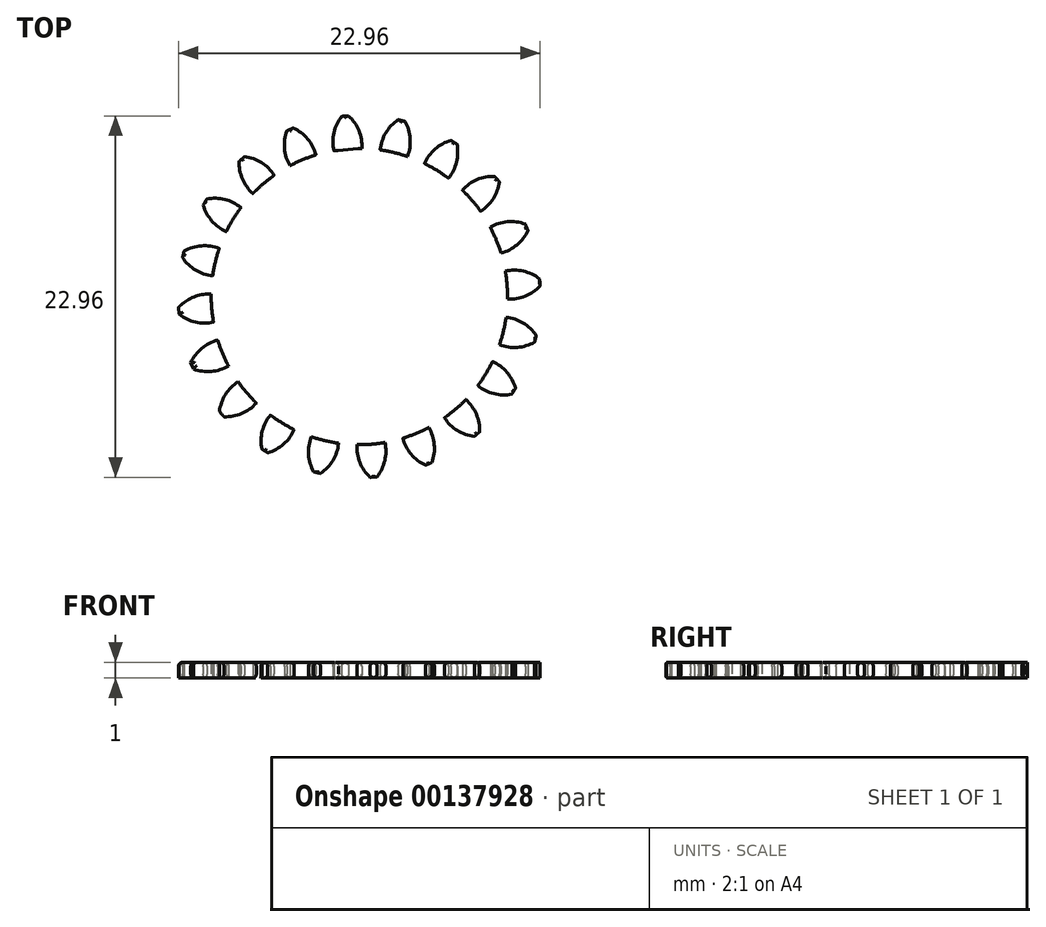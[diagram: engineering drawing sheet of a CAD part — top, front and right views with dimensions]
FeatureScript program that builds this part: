
annotation { "Feature Type Name" : "Feature", "Feature Type Description" : "" }
export const myFeature = defineFeature(function(context is Context, id is Id, definition is map)
    precondition{}
    {
        {
            assignVariable(context, id + "F0", {"name" : "GearDepth", "anyValue" : 1});
        }
        {
            assignVariable(context, id + "F1", {"name" : "TeethFillet", "anyValue" : getVariable(context, 'GearDepth') * .25});
        }
        {
            var Q0;
            Q0=qCreatedBy(makeId("Top.planeOp"),FACE);
            var sketch = newSketch(context, id + "F2", { "sketchPlane" : qUnion([Q0])});
            skCircle(sketch, "E0", {"center": v(0, 0) * mm, "radius": 9.4 * mm});
            skCircle(sketch, "E1", {"center": v(0, 0) * mm, "radius": 10.45 * mm, "construction": true});
            skCircle(sketch, "E2", {"center": v(0, 0) * mm, "radius": 11.5 * mm, "construction": true});
            skLineSegment(sketch, "E3", {"start": v(0, 0) * mm, "end": v(0, 17.6) * mm, "construction": true});
            skLineSegment(sketch, "E4", {"start": v(0, 0) * mm, "end": v(-1.42, 18) * mm, "construction": true});
            skLineSegment(sketch, "E5", {"start": v(0, 10.45) * mm, "end": v(-10.54, 10.45) * mm, "construction": true});
            skLineSegment(sketch, "E6", {"start": v(0, 10.45) * mm, "end": v(-10.3, 6.7) * mm, "construction": true});
            skCircle(sketch, "E7", {"center": v(0, 10.45) * mm, "radius": 2.61 * mm, "construction": true});
            skCircle(sketch, "E8", {"center": v(-2.46, 9.56) * mm, "radius": 2.61 * mm, "construction": true});
            skArc(sketch, "E9", {"start": v(-4.91, 10.45) * mm, "mid": v(-4.92, 10.42) * mm, "end": v(-4.94, 10.39) * mm});
            skArc(sketch, "E10.trimOffspring", {"start": v(0.15, 9.4) * mm, "mid": v(-0.03, 10.54) * mm, "end": v(-0.68, 11.48) * mm});
            skArc(sketch, "E11.MirrorCS", {"start": v(-1.62, 9.27) * mm, "mid": v(-1.62, 10.41) * mm, "end": v(-1.12, 11.45) * mm});
            skLineSegment(sketch, "E12", {"start": v(-1.12, 11.45) * mm, "end": v(-0.68, 11.48) * mm});
            skArc(sketch, "E13.1.0", {"start": v(-2.76, 9) * mm, "mid": v(-3.29, 10.01) * mm, "end": v(-4.2, 10.7) * mm});
            skLineSegment(sketch, "E13.1.1", {"start": v(-4.6, 10.54) * mm, "end": v(-4.2, 10.7) * mm});
            skArc(sketch, "E13.1.2", {"start": v(-4.4, 8.31) * mm, "mid": v(-4.76, 9.4) * mm, "end": v(-4.6, 10.54) * mm});
            skArc(sketch, "E13.2.0", {"start": v(-5.4, 7.7) * mm, "mid": v(-6.22, 8.5) * mm, "end": v(-7.3, 8.89) * mm});
            skLineSegment(sketch, "E13.2.1", {"start": v(-7.64, 8.6) * mm, "end": v(-7.3, 8.89) * mm});
            skArc(sketch, "E13.2.2", {"start": v(-6.76, 6.54) * mm, "mid": v(-7.43, 7.47) * mm, "end": v(-7.64, 8.6) * mm});
            skArc(sketch, "E13.3.0", {"start": v(-7.52, 5.65) * mm, "mid": v(-8.54, 6.17) * mm, "end": v(-9.69, 6.2) * mm});
            skLineSegment(sketch, "E13.3.1", {"start": v(-9.92, 5.82) * mm, "end": v(-9.69, 6.2) * mm});
            skArc(sketch, "E13.3.2", {"start": v(-8.45, 4.13) * mm, "mid": v(-9.37, 4.81) * mm, "end": v(-9.92, 5.82) * mm});
            skArc(sketch, "E13.4.0", {"start": v(-8.9, 3.05) * mm, "mid": v(-10.03, 3.23) * mm, "end": v(-11.13, 2.9) * mm});
            skLineSegment(sketch, "E13.4.1", {"start": v(-11.23, 2.47) * mm, "end": v(-11.13, 2.9) * mm});
            skArc(sketch, "E13.4.2", {"start": v(-9.32, 1.32) * mm, "mid": v(-10.4, 1.68) * mm, "end": v(-11.23, 2.47) * mm});
            skArc(sketch, "E13.5.0", {"start": v(-9.4, 0.15) * mm, "mid": v(-10.54, -0.03) * mm, "end": v(-11.48, -0.68) * mm});
            skLineSegment(sketch, "E13.5.1", {"start": v(-11.45, -1.12) * mm, "end": v(-11.48, -0.68) * mm});
            skArc(sketch, "E13.5.2", {"start": v(-9.27, -1.62) * mm, "mid": v(-10.41, -1.62) * mm, "end": v(-11.45, -1.12) * mm});
            skArc(sketch, "E13.6.0", {"start": v(-9, -2.76) * mm, "mid": v(-10.01, -3.29) * mm, "end": v(-10.7, -4.2) * mm});
            skLineSegment(sketch, "E13.6.1", {"start": v(-10.54, -4.6) * mm, "end": v(-10.7, -4.2) * mm});
            skArc(sketch, "E13.6.2", {"start": v(-8.31, -4.4) * mm, "mid": v(-9.4, -4.76) * mm, "end": v(-10.54, -4.6) * mm});
            skArc(sketch, "E13.7.0", {"start": v(-7.7, -5.4) * mm, "mid": v(-8.5, -6.22) * mm, "end": v(-8.89, -7.3) * mm});
            skLineSegment(sketch, "E13.7.1", {"start": v(-8.6, -7.64) * mm, "end": v(-8.89, -7.3) * mm});
            skArc(sketch, "E13.7.2", {"start": v(-6.54, -6.76) * mm, "mid": v(-7.47, -7.43) * mm, "end": v(-8.6, -7.64) * mm});
            skArc(sketch, "E13.8.0", {"start": v(-5.65, -7.52) * mm, "mid": v(-6.17, -8.54) * mm, "end": v(-6.2, -9.69) * mm});
            skLineSegment(sketch, "E13.8.1", {"start": v(-5.82, -9.92) * mm, "end": v(-6.2, -9.69) * mm});
            skArc(sketch, "E13.8.2", {"start": v(-4.13, -8.45) * mm, "mid": v(-4.81, -9.37) * mm, "end": v(-5.82, -9.92) * mm});
            skArc(sketch, "E13.9.0", {"start": v(-3.05, -8.9) * mm, "mid": v(-3.23, -10.03) * mm, "end": v(-2.9, -11.13) * mm});
            skLineSegment(sketch, "E13.9.1", {"start": v(-2.47, -11.23) * mm, "end": v(-2.9, -11.13) * mm});
            skArc(sketch, "E13.9.2", {"start": v(-1.32, -9.32) * mm, "mid": v(-1.68, -10.4) * mm, "end": v(-2.47, -11.23) * mm});
            skArc(sketch, "E13.10.0", {"start": v(-0.15, -9.4) * mm, "mid": v(0.03, -10.54) * mm, "end": v(0.68, -11.48) * mm});
            skLineSegment(sketch, "E13.10.1", {"start": v(1.12, -11.45) * mm, "end": v(0.68, -11.48) * mm});
            skArc(sketch, "E13.10.2", {"start": v(1.62, -9.27) * mm, "mid": v(1.62, -10.41) * mm, "end": v(1.12, -11.45) * mm});
            skArc(sketch, "E13.11.0", {"start": v(2.76, -9) * mm, "mid": v(3.29, -10.01) * mm, "end": v(4.2, -10.7) * mm});
            skLineSegment(sketch, "E13.11.1", {"start": v(4.6, -10.54) * mm, "end": v(4.2, -10.7) * mm});
            skArc(sketch, "E13.11.2", {"start": v(4.4, -8.31) * mm, "mid": v(4.76, -9.4) * mm, "end": v(4.6, -10.54) * mm});
            skArc(sketch, "E13.12.0", {"start": v(5.4, -7.7) * mm, "mid": v(6.22, -8.5) * mm, "end": v(7.3, -8.89) * mm});
            skLineSegment(sketch, "E13.12.1", {"start": v(7.64, -8.6) * mm, "end": v(7.3, -8.89) * mm});
            skArc(sketch, "E13.12.2", {"start": v(6.76, -6.54) * mm, "mid": v(7.43, -7.47) * mm, "end": v(7.64, -8.6) * mm});
            skArc(sketch, "E13.13.0", {"start": v(7.52, -5.65) * mm, "mid": v(8.54, -6.17) * mm, "end": v(9.69, -6.2) * mm});
            skLineSegment(sketch, "E13.13.1", {"start": v(9.92, -5.82) * mm, "end": v(9.69, -6.2) * mm});
            skArc(sketch, "E13.13.2", {"start": v(8.45, -4.13) * mm, "mid": v(9.37, -4.81) * mm, "end": v(9.92, -5.82) * mm});
            skArc(sketch, "E13.14.0", {"start": v(8.9, -3.05) * mm, "mid": v(10.03, -3.23) * mm, "end": v(11.13, -2.9) * mm});
            skLineSegment(sketch, "E13.14.1", {"start": v(11.23, -2.47) * mm, "end": v(11.13, -2.9) * mm});
            skArc(sketch, "E13.14.2", {"start": v(9.32, -1.32) * mm, "mid": v(10.4, -1.68) * mm, "end": v(11.23, -2.47) * mm});
            skArc(sketch, "E13.15.0", {"start": v(9.4, -0.15) * mm, "mid": v(10.54, 0.03) * mm, "end": v(11.48, 0.68) * mm});
            skLineSegment(sketch, "E13.15.1", {"start": v(11.45, 1.12) * mm, "end": v(11.48, 0.68) * mm});
            skArc(sketch, "E13.15.2", {"start": v(9.27, 1.62) * mm, "mid": v(10.41, 1.62) * mm, "end": v(11.45, 1.12) * mm});
            skArc(sketch, "E13.16.0", {"start": v(9, 2.76) * mm, "mid": v(10.01, 3.29) * mm, "end": v(10.7, 4.2) * mm});
            skLineSegment(sketch, "E13.16.1", {"start": v(10.54, 4.6) * mm, "end": v(10.7, 4.2) * mm});
            skArc(sketch, "E13.16.2", {"start": v(8.31, 4.4) * mm, "mid": v(9.4, 4.76) * mm, "end": v(10.54, 4.6) * mm});
            skArc(sketch, "E13.17.0", {"start": v(7.7, 5.4) * mm, "mid": v(8.5, 6.22) * mm, "end": v(8.89, 7.3) * mm});
            skLineSegment(sketch, "E13.17.1", {"start": v(8.6, 7.64) * mm, "end": v(8.89, 7.3) * mm});
            skArc(sketch, "E13.17.2", {"start": v(6.54, 6.76) * mm, "mid": v(7.47, 7.43) * mm, "end": v(8.6, 7.64) * mm});
            skArc(sketch, "E13.18.0", {"start": v(5.65, 7.52) * mm, "mid": v(6.17, 8.54) * mm, "end": v(6.2, 9.69) * mm});
            skLineSegment(sketch, "E13.18.1", {"start": v(5.82, 9.92) * mm, "end": v(6.2, 9.69) * mm});
            skArc(sketch, "E13.18.2", {"start": v(4.13, 8.45) * mm, "mid": v(4.81, 9.37) * mm, "end": v(5.82, 9.92) * mm});
            skArc(sketch, "E13.19.0", {"start": v(3.05, 8.9) * mm, "mid": v(3.23, 10.03) * mm, "end": v(2.9, 11.13) * mm});
            skLineSegment(sketch, "E13.19.1", {"start": v(2.47, 11.23) * mm, "end": v(2.9, 11.13) * mm});
            skArc(sketch, "E13.19.2", {"start": v(1.32, 9.32) * mm, "mid": v(1.68, 10.4) * mm, "end": v(2.47, 11.23) * mm});
            skCircle(sketch, "E14", {"center": v(0, 0) * mm, "radius": 2.5 * mm});
            skLineSegment(sketch, "E15", {"start": v(-1.62, 9.27) * mm, "end": v(0.15, 9.4) * mm});
            skSolve(sketch);
        }
        {
            var Q0;
            {var subQ0=sQuery(id+"F2.wireOp",EDGE,"E10.trimOffspring");Q0=makeQuery(id+"F2.imprint","IMPRINT",FACE,{"disambiguationData":[TD([[makeQuery(id+"F2.imprint","IMPRINT",EDGE,{"derivedFrom":subQ0}),1.0]])]});}
            var Q1;
            {var subQ0=sQuery(id+"F2.wireOp",EDGE,"E0");var subQ1=makeQuery(id+"F2.imprint","INTERSECT",VERTEX,{"derivedFrom":[subQ0,sQuery(id+"F2.wireOp",EDGE,"E10.trimOffspring")]});Q1=makeQuery(id+"F2.imprint","IMPRINT",FACE,{"disambiguationData":[TD([[makeQuery(id+"F2.imprint","IMPRINT",EDGE,{"disambiguationData":[TD([[subQ1,-1.0]])],"derivedFrom":subQ0}),1.0]])]});}
            var Q2;
            {var subQ0=sQuery(id+"F2.wireOp",EDGE,"E13.1.0");Q2=makeQuery(id+"F2.imprint","IMPRINT",FACE,{"disambiguationData":[TD([[makeQuery(id+"F2.imprint","IMPRINT",EDGE,{"derivedFrom":subQ0}),1.0]])]});}
            var Q3;
            {var subQ0=sQuery(id+"F2.wireOp",EDGE,"E13.2.0");Q3=makeQuery(id+"F2.imprint","IMPRINT",FACE,{"disambiguationData":[TD([[makeQuery(id+"F2.imprint","IMPRINT",EDGE,{"derivedFrom":subQ0}),1.0]])]});}
            var Q4;
            {var subQ0=sQuery(id+"F2.wireOp",EDGE,"E13.3.0");Q4=makeQuery(id+"F2.imprint","IMPRINT",FACE,{"disambiguationData":[TD([[makeQuery(id+"F2.imprint","IMPRINT",EDGE,{"derivedFrom":subQ0}),1.0]])]});}
            var Q5;
            {var subQ0=sQuery(id+"F2.wireOp",EDGE,"E13.4.0");Q5=makeQuery(id+"F2.imprint","IMPRINT",FACE,{"disambiguationData":[TD([[makeQuery(id+"F2.imprint","IMPRINT",EDGE,{"derivedFrom":subQ0}),1.0]])]});}
            var Q6;
            {var subQ0=sQuery(id+"F2.wireOp",EDGE,"E13.5.0");Q6=makeQuery(id+"F2.imprint","IMPRINT",FACE,{"disambiguationData":[TD([[makeQuery(id+"F2.imprint","IMPRINT",EDGE,{"derivedFrom":subQ0}),1.0]])]});}
            var Q7;
            {var subQ0=sQuery(id+"F2.wireOp",EDGE,"E13.6.0");Q7=makeQuery(id+"F2.imprint","IMPRINT",FACE,{"disambiguationData":[TD([[makeQuery(id+"F2.imprint","IMPRINT",EDGE,{"derivedFrom":subQ0}),1.0]])]});}
            var Q8;
            {var subQ0=sQuery(id+"F2.wireOp",EDGE,"E13.7.0");Q8=makeQuery(id+"F2.imprint","IMPRINT",FACE,{"disambiguationData":[TD([[makeQuery(id+"F2.imprint","IMPRINT",EDGE,{"derivedFrom":subQ0}),1.0]])]});}
            var Q9;
            {var subQ0=sQuery(id+"F2.wireOp",EDGE,"E13.8.0");Q9=makeQuery(id+"F2.imprint","IMPRINT",FACE,{"disambiguationData":[TD([[makeQuery(id+"F2.imprint","IMPRINT",EDGE,{"derivedFrom":subQ0}),1.0]])]});}
            var Q10;
            {var subQ0=sQuery(id+"F2.wireOp",EDGE,"E13.9.0");Q10=makeQuery(id+"F2.imprint","IMPRINT",FACE,{"disambiguationData":[TD([[makeQuery(id+"F2.imprint","IMPRINT",EDGE,{"derivedFrom":subQ0}),1.0]])]});}
            var Q11;
            {var subQ0=sQuery(id+"F2.wireOp",EDGE,"E13.10.0");Q11=makeQuery(id+"F2.imprint","IMPRINT",FACE,{"disambiguationData":[TD([[makeQuery(id+"F2.imprint","IMPRINT",EDGE,{"derivedFrom":subQ0}),1.0]])]});}
            var Q12;
            {var subQ0=sQuery(id+"F2.wireOp",EDGE,"E13.11.0");Q12=makeQuery(id+"F2.imprint","IMPRINT",FACE,{"disambiguationData":[TD([[makeQuery(id+"F2.imprint","IMPRINT",EDGE,{"derivedFrom":subQ0}),1.0]])]});}
            var Q13;
            {var subQ0=sQuery(id+"F2.wireOp",EDGE,"E13.12.0");Q13=makeQuery(id+"F2.imprint","IMPRINT",FACE,{"disambiguationData":[TD([[makeQuery(id+"F2.imprint","IMPRINT",EDGE,{"derivedFrom":subQ0}),1.0]])]});}
            var Q14;
            {var subQ0=sQuery(id+"F2.wireOp",EDGE,"E13.13.0");Q14=makeQuery(id+"F2.imprint","IMPRINT",FACE,{"disambiguationData":[TD([[makeQuery(id+"F2.imprint","IMPRINT",EDGE,{"derivedFrom":subQ0}),1.0]])]});}
            var Q15;
            {var subQ0=sQuery(id+"F2.wireOp",EDGE,"E13.14.0");Q15=makeQuery(id+"F2.imprint","IMPRINT",FACE,{"disambiguationData":[TD([[makeQuery(id+"F2.imprint","IMPRINT",EDGE,{"derivedFrom":subQ0}),1.0]])]});}
            var Q16;
            {var subQ0=sQuery(id+"F2.wireOp",EDGE,"E13.15.0");Q16=makeQuery(id+"F2.imprint","IMPRINT",FACE,{"disambiguationData":[TD([[makeQuery(id+"F2.imprint","IMPRINT",EDGE,{"derivedFrom":subQ0}),1.0]])]});}
            var Q17;
            {var subQ0=sQuery(id+"F2.wireOp",EDGE,"E13.16.0");Q17=makeQuery(id+"F2.imprint","IMPRINT",FACE,{"disambiguationData":[TD([[makeQuery(id+"F2.imprint","IMPRINT",EDGE,{"derivedFrom":subQ0}),1.0]])]});}
            var Q18;
            {var subQ0=sQuery(id+"F2.wireOp",EDGE,"E13.17.0");Q18=makeQuery(id+"F2.imprint","IMPRINT",FACE,{"disambiguationData":[TD([[makeQuery(id+"F2.imprint","IMPRINT",EDGE,{"derivedFrom":subQ0}),1.0]])]});}
            var Q19;
            {var subQ0=sQuery(id+"F2.wireOp",EDGE,"E13.18.0");Q19=makeQuery(id+"F2.imprint","IMPRINT",FACE,{"disambiguationData":[TD([[makeQuery(id+"F2.imprint","IMPRINT",EDGE,{"derivedFrom":subQ0}),1.0]])]});}
            var Q20;
            {var subQ0=sQuery(id+"F2.wireOp",EDGE,"E13.19.0");Q20=makeQuery(id+"F2.imprint","IMPRINT",FACE,{"disambiguationData":[TD([[makeQuery(id+"F2.imprint","IMPRINT",EDGE,{"derivedFrom":subQ0}),1.0]])]});}
            var Q21;
            Q21=sQuery(id+"F2.wireOp",EDGE,"E0");
            var Q22;
            Q22=sQuery(id+"F2.wireOp",EDGE,"E10.trimOffspring");
            var Q23;
            Q23=sQuery(id+"F2.wireOp",EDGE,"E12");
            var Q24;
            Q24=sQuery(id+"F2.wireOp",EDGE,"E11.MirrorCS");
            extrude(context, id + "F3", {"entities" : qUnion([Q0, Q1, Q2, Q3, Q4, Q5, Q6, Q7, Q8, Q9, Q10, Q11, Q12, Q13, Q14, Q15, Q16, Q17, Q18, Q19, Q20]), "surfaceEntities" : qUnion([Q21, Q22, Q23, Q24]), "depth" : (getVariable(context, 'GearDepth')) * mm});
        }
        {
            var Q0;
            Q0=makeQuery(id+"F3.opExtrude","CAP_EDGE",EDGE,{"disambiguationData":[OSD([sQuery(id+"F2.wireOp",EDGE,"E13.5.2")])],"isStart":false});
            var Q1;
            Q1=makeQuery(id+"F3.opExtrude","CAP_EDGE",EDGE,{"disambiguationData":[OSD([sQuery(id+"F2.wireOp",EDGE,"E13.5.1")])],"isStart":false});
            var Q2;
            {var subQ0=sQuery(id+"F2.wireOp",EDGE,"E0");Q2=makeQuery(id+"F3.opExtrude","CAP_EDGE",EDGE,{"disambiguationData":[OSD([subQ0]),TDD([makeQuery(id+"F2.imprint","IMPRINT",EDGE,{"disambiguationData":[TD([[makeQuery(id+"F2.imprint","INTERSECT",VERTEX,{"derivedFrom":[subQ0,sQuery(id+"F2.wireOp",EDGE,"E13.5.2")]}),-1.0]])],"derivedFrom":subQ0})])],"isStart":false});}
            var Q3;
            Q3=makeQuery(id+"F3.opExtrude","CAP_EDGE",EDGE,{"disambiguationData":[OSD([sQuery(id+"F2.wireOp",EDGE,"E13.6.0")])],"isStart":false});
            var Q4;
            Q4=makeQuery(id+"F3.opExtrude","CAP_EDGE",EDGE,{"disambiguationData":[OSD([sQuery(id+"F2.wireOp",EDGE,"E13.6.1")])],"isStart":false});
            var Q5;
            Q5=makeQuery(id+"F3.opExtrude","CAP_EDGE",EDGE,{"disambiguationData":[OSD([sQuery(id+"F2.wireOp",EDGE,"E13.6.2")])],"isStart":false});
            var Q6;
            {var subQ0=sQuery(id+"F2.wireOp",EDGE,"E0");Q6=makeQuery(id+"F3.opExtrude","SWEPT_FACE",FACE,{"disambiguationData":[OSD([subQ0]),TDD([makeQuery(id+"F2.imprint","IMPRINT",EDGE,{"disambiguationData":[TD([[makeQuery(id+"F2.imprint","INTERSECT",VERTEX,{"derivedFrom":[subQ0,sQuery(id+"F2.wireOp",EDGE,"E13.6.2")]}),-1.0]])],"derivedFrom":subQ0})])]});}
            var Q7;
            {var subQ0=sQuery(id+"F2.wireOp",EDGE,"E0");Q7=makeQuery(id+"F3.opExtrude","CAP_EDGE",EDGE,{"disambiguationData":[OSD([subQ0]),TDD([makeQuery(id+"F2.imprint","IMPRINT",EDGE,{"disambiguationData":[TD([[makeQuery(id+"F2.imprint","INTERSECT",VERTEX,{"derivedFrom":[subQ0,sQuery(id+"F2.wireOp",EDGE,"E13.6.2")]}),-1.0]])],"derivedFrom":subQ0})])],"isStart":false});}
            var Q8;
            Q8=makeQuery(id+"F3.opExtrude","CAP_EDGE",EDGE,{"disambiguationData":[OSD([sQuery(id+"F2.wireOp",EDGE,"E13.7.2")])],"isStart":true});
            var Q9;
            {var subQ0=sQuery(id+"F2.wireOp",EDGE,"E0");Q9=makeQuery(id+"F3.opExtrude","CAP_EDGE",EDGE,{"disambiguationData":[OSD([subQ0]),TDD([makeQuery(id+"F2.imprint","IMPRINT",EDGE,{"disambiguationData":[TD([[makeQuery(id+"F2.imprint","INTERSECT",VERTEX,{"derivedFrom":[subQ0,sQuery(id+"F2.wireOp",EDGE,"E13.7.2")]}),-1.0]])],"derivedFrom":subQ0})])],"isStart":true});}
            var Q10;
            Q10=makeQuery(id+"F3.opExtrude","CAP_EDGE",EDGE,{"disambiguationData":[OSD([sQuery(id+"F2.wireOp",EDGE,"E13.7.2")])],"isStart":false});
            var Q11;
            {var subQ0=sQuery(id+"F2.wireOp",EDGE,"E0");Q11=makeQuery(id+"F3.opExtrude","CAP_EDGE",EDGE,{"disambiguationData":[OSD([subQ0]),TDD([makeQuery(id+"F2.imprint","IMPRINT",EDGE,{"disambiguationData":[TD([[makeQuery(id+"F2.imprint","INTERSECT",VERTEX,{"derivedFrom":[subQ0,sQuery(id+"F2.wireOp",EDGE,"E13.7.2")]}),-1.0]])],"derivedFrom":subQ0})])],"isStart":false});}
            var Q12;
            Q12=makeQuery(id+"F3.opExtrude","CAP_EDGE",EDGE,{"disambiguationData":[OSD([sQuery(id+"F2.wireOp",EDGE,"E13.8.0")])],"isStart":false});
            var Q13;
            {var subQ0=sQuery(id+"F2.wireOp",EDGE,"E0");Q13=makeQuery(id+"F3.opExtrude","SWEPT_FACE",FACE,{"disambiguationData":[OSD([subQ0]),TDD([makeQuery(id+"F2.imprint","IMPRINT",EDGE,{"disambiguationData":[TD([[makeQuery(id+"F2.imprint","INTERSECT",VERTEX,{"derivedFrom":[subQ0,sQuery(id+"F2.wireOp",EDGE,"E13.7.2")]}),-1.0]])],"derivedFrom":subQ0})])]});}
            var Q14;
            Q14=makeQuery(id+"F3.opExtrude","CAP_EDGE",EDGE,{"disambiguationData":[OSD([sQuery(id+"F2.wireOp",EDGE,"E13.6.0")])],"isStart":true});
            var Q15;
            Q15=makeQuery(id+"F3.opExtrude","CAP_EDGE",EDGE,{"disambiguationData":[OSD([sQuery(id+"F2.wireOp",EDGE,"E13.8.2")])],"isStart":false});
            var Q16;
            {var subQ0=sQuery(id+"F2.wireOp",EDGE,"E0");Q16=makeQuery(id+"F3.opExtrude","CAP_EDGE",EDGE,{"disambiguationData":[OSD([subQ0]),TDD([makeQuery(id+"F2.imprint","IMPRINT",EDGE,{"disambiguationData":[TD([[makeQuery(id+"F2.imprint","INTERSECT",VERTEX,{"derivedFrom":[subQ0,sQuery(id+"F2.wireOp",EDGE,"E13.8.2")]}),-1.0]])],"derivedFrom":subQ0})])],"isStart":false});}
            var Q17;
            Q17=makeQuery(id+"F3.opExtrude","CAP_EDGE",EDGE,{"disambiguationData":[OSD([sQuery(id+"F2.wireOp",EDGE,"E13.9.0")])],"isStart":false});
            var Q18;
            Q18=makeQuery(id+"F3.opExtrude","CAP_EDGE",EDGE,{"disambiguationData":[OSD([sQuery(id+"F2.wireOp",EDGE,"E13.9.2")])],"isStart":false});
            var Q19;
            {var subQ0=sQuery(id+"F2.wireOp",EDGE,"E0");Q19=makeQuery(id+"F3.opExtrude","CAP_EDGE",EDGE,{"disambiguationData":[OSD([subQ0]),TDD([makeQuery(id+"F2.imprint","IMPRINT",EDGE,{"disambiguationData":[TD([[makeQuery(id+"F2.imprint","INTERSECT",VERTEX,{"derivedFrom":[subQ0,sQuery(id+"F2.wireOp",EDGE,"E13.9.2")]}),-1.0]])],"derivedFrom":subQ0})])],"isStart":false});}
            var Q20;
            Q20=makeQuery(id+"F3.opExtrude","CAP_EDGE",EDGE,{"disambiguationData":[OSD([sQuery(id+"F2.wireOp",EDGE,"E13.10.0")])],"isStart":false});
            var Q21;
            Q21=makeQuery(id+"F3.opExtrude","CAP_EDGE",EDGE,{"disambiguationData":[OSD([sQuery(id+"F2.wireOp",EDGE,"E13.10.2")])],"isStart":false});
            var Q22;
            {var subQ0=sQuery(id+"F2.wireOp",EDGE,"E0");Q22=makeQuery(id+"F3.opExtrude","CAP_EDGE",EDGE,{"disambiguationData":[OSD([subQ0]),TDD([makeQuery(id+"F2.imprint","IMPRINT",EDGE,{"disambiguationData":[TD([[makeQuery(id+"F2.imprint","INTERSECT",VERTEX,{"derivedFrom":[subQ0,sQuery(id+"F2.wireOp",EDGE,"E13.10.2")]}),-1.0]])],"derivedFrom":subQ0})])],"isStart":false});}
            var Q23;
            Q23=makeQuery(id+"F3.opExtrude","CAP_EDGE",EDGE,{"disambiguationData":[OSD([sQuery(id+"F2.wireOp",EDGE,"E13.11.0")])],"isStart":false});
            var Q24;
            Q24=makeQuery(id+"F3.opExtrude","CAP_EDGE",EDGE,{"disambiguationData":[OSD([sQuery(id+"F2.wireOp",EDGE,"E13.11.2")])],"isStart":false});
            var Q25;
            {var subQ0=sQuery(id+"F2.wireOp",EDGE,"E0");Q25=makeQuery(id+"F3.opExtrude","CAP_EDGE",EDGE,{"disambiguationData":[OSD([subQ0]),TDD([makeQuery(id+"F2.imprint","IMPRINT",EDGE,{"disambiguationData":[TD([[makeQuery(id+"F2.imprint","INTERSECT",VERTEX,{"derivedFrom":[subQ0,sQuery(id+"F2.wireOp",EDGE,"E13.11.2")]}),-1.0]])],"derivedFrom":subQ0})])],"isStart":false});}
            var Q26;
            Q26=makeQuery(id+"F3.opExtrude","CAP_EDGE",EDGE,{"disambiguationData":[OSD([sQuery(id+"F2.wireOp",EDGE,"E13.12.0")])],"isStart":false});
            var Q27;
            Q27=makeQuery(id+"F3.opExtrude","CAP_EDGE",EDGE,{"disambiguationData":[OSD([sQuery(id+"F2.wireOp",EDGE,"E13.12.2")])],"isStart":false});
            var Q28;
            {var subQ0=sQuery(id+"F2.wireOp",EDGE,"E0");Q28=makeQuery(id+"F3.opExtrude","CAP_EDGE",EDGE,{"disambiguationData":[OSD([subQ0]),TDD([makeQuery(id+"F2.imprint","IMPRINT",EDGE,{"disambiguationData":[TD([[makeQuery(id+"F2.imprint","INTERSECT",VERTEX,{"derivedFrom":[subQ0,sQuery(id+"F2.wireOp",EDGE,"E13.12.2")]}),-1.0]])],"derivedFrom":subQ0})])],"isStart":false});}
            var Q29;
            Q29=makeQuery(id+"F3.opExtrude","CAP_EDGE",EDGE,{"disambiguationData":[OSD([sQuery(id+"F2.wireOp",EDGE,"E13.13.0")])],"isStart":false});
            var Q30;
            Q30=makeQuery(id+"F3.opExtrude","CAP_EDGE",EDGE,{"disambiguationData":[OSD([sQuery(id+"F2.wireOp",EDGE,"E13.13.2")])],"isStart":false});
            var Q31;
            {var subQ0=sQuery(id+"F2.wireOp",EDGE,"E0");Q31=makeQuery(id+"F3.opExtrude","CAP_EDGE",EDGE,{"disambiguationData":[OSD([subQ0]),TDD([makeQuery(id+"F2.imprint","IMPRINT",EDGE,{"disambiguationData":[TD([[makeQuery(id+"F2.imprint","INTERSECT",VERTEX,{"derivedFrom":[subQ0,sQuery(id+"F2.wireOp",EDGE,"E13.13.2")]}),-1.0]])],"derivedFrom":subQ0})])],"isStart":false});}
            var Q32;
            Q32=makeQuery(id+"F3.opExtrude","CAP_EDGE",EDGE,{"disambiguationData":[OSD([sQuery(id+"F2.wireOp",EDGE,"E13.14.0")])],"isStart":false});
            var Q33;
            Q33=makeQuery(id+"F3.opExtrude","CAP_EDGE",EDGE,{"disambiguationData":[OSD([sQuery(id+"F2.wireOp",EDGE,"E13.14.2")])],"isStart":false});
            var Q34;
            {var subQ0=sQuery(id+"F2.wireOp",EDGE,"E0");Q34=makeQuery(id+"F3.opExtrude","CAP_EDGE",EDGE,{"disambiguationData":[OSD([subQ0]),TDD([makeQuery(id+"F2.imprint","IMPRINT",EDGE,{"disambiguationData":[TD([[makeQuery(id+"F2.imprint","INTERSECT",VERTEX,{"derivedFrom":[subQ0,sQuery(id+"F2.wireOp",EDGE,"E13.14.2")]}),-1.0]])],"derivedFrom":subQ0})])],"isStart":false});}
            var Q35;
            Q35=makeQuery(id+"F3.opExtrude","CAP_EDGE",EDGE,{"disambiguationData":[OSD([sQuery(id+"F2.wireOp",EDGE,"E13.15.0")])],"isStart":false});
            var Q36;
            {var subQ0=sQuery(id+"F2.wireOp",EDGE,"E0");Q36=makeQuery(id+"F3.opExtrude","CAP_EDGE",EDGE,{"disambiguationData":[OSD([subQ0]),TDD([makeQuery(id+"F2.imprint","IMPRINT",EDGE,{"disambiguationData":[TD([[makeQuery(id+"F2.imprint","INTERSECT",VERTEX,{"derivedFrom":[subQ0,sQuery(id+"F2.wireOp",EDGE,"E13.14.2")]}),-1.0]])],"derivedFrom":subQ0})])],"isStart":false});}
            var Q37;
            Q37=makeQuery(id+"F3.opExtrude","CAP_EDGE",EDGE,{"disambiguationData":[OSD([sQuery(id+"F2.wireOp",EDGE,"E13.15.2")])],"isStart":false});
            var Q38;
            {var subQ0=sQuery(id+"F2.wireOp",EDGE,"E0");Q38=makeQuery(id+"F3.opExtrude","CAP_EDGE",EDGE,{"disambiguationData":[OSD([subQ0]),TDD([makeQuery(id+"F2.imprint","IMPRINT",EDGE,{"disambiguationData":[TD([[makeQuery(id+"F2.imprint","INTERSECT",VERTEX,{"derivedFrom":[subQ0,sQuery(id+"F2.wireOp",EDGE,"E13.15.2")]}),-1.0]])],"derivedFrom":subQ0})])],"isStart":false});}
            var Q39;
            Q39=makeQuery(id+"F3.opExtrude","CAP_EDGE",EDGE,{"disambiguationData":[OSD([sQuery(id+"F2.wireOp",EDGE,"E13.16.0")])],"isStart":false});
            var Q40;
            Q40=makeQuery(id+"F3.opExtrude","CAP_EDGE",EDGE,{"disambiguationData":[OSD([sQuery(id+"F2.wireOp",EDGE,"E13.16.2")])],"isStart":false});
            var Q41;
            Q41=makeQuery(id+"F3.opExtrude","CAP_EDGE",EDGE,{"disambiguationData":[OSD([sQuery(id+"F2.wireOp",EDGE,"E13.17.0")])],"isStart":false});
            var Q42;
            {var subQ0=sQuery(id+"F2.wireOp",EDGE,"E0");Q42=makeQuery(id+"F3.opExtrude","CAP_EDGE",EDGE,{"disambiguationData":[OSD([subQ0]),TDD([makeQuery(id+"F2.imprint","IMPRINT",EDGE,{"disambiguationData":[TD([[makeQuery(id+"F2.imprint","INTERSECT",VERTEX,{"derivedFrom":[subQ0,sQuery(id+"F2.wireOp",EDGE,"E13.16.2")]}),-1.0]])],"derivedFrom":subQ0})])],"isStart":false});}
            var Q43;
            Q43=makeQuery(id+"F3.opExtrude","CAP_EDGE",EDGE,{"disambiguationData":[OSD([sQuery(id+"F2.wireOp",EDGE,"E13.17.2")])],"isStart":false});
            var Q44;
            {var subQ0=sQuery(id+"F2.wireOp",EDGE,"E0");Q44=makeQuery(id+"F3.opExtrude","CAP_EDGE",EDGE,{"disambiguationData":[OSD([subQ0]),TDD([makeQuery(id+"F2.imprint","IMPRINT",EDGE,{"disambiguationData":[TD([[makeQuery(id+"F2.imprint","INTERSECT",VERTEX,{"derivedFrom":[subQ0,sQuery(id+"F2.wireOp",EDGE,"E13.17.2")]}),-1.0]])],"derivedFrom":subQ0})])],"isStart":false});}
            var Q45;
            Q45=makeQuery(id+"F3.opExtrude","CAP_EDGE",EDGE,{"disambiguationData":[OSD([sQuery(id+"F2.wireOp",EDGE,"E13.18.0")])],"isStart":false});
            var Q46;
            Q46=makeQuery(id+"F3.opExtrude","CAP_EDGE",EDGE,{"disambiguationData":[OSD([sQuery(id+"F2.wireOp",EDGE,"E13.18.2")])],"isStart":false});
            var Q47;
            {var subQ0=sQuery(id+"F2.wireOp",EDGE,"E0");Q47=makeQuery(id+"F3.opExtrude","CAP_EDGE",EDGE,{"disambiguationData":[OSD([subQ0]),TDD([makeQuery(id+"F2.imprint","IMPRINT",EDGE,{"disambiguationData":[TD([[makeQuery(id+"F2.imprint","INTERSECT",VERTEX,{"derivedFrom":[subQ0,sQuery(id+"F2.wireOp",EDGE,"E13.18.2")]}),-1.0]])],"derivedFrom":subQ0})])],"isStart":false});}
            var Q48;
            Q48=makeQuery(id+"F3.opExtrude","CAP_EDGE",EDGE,{"disambiguationData":[OSD([sQuery(id+"F2.wireOp",EDGE,"E13.19.0")])],"isStart":false});
            var Q49;
            Q49=makeQuery(id+"F3.opExtrude","CAP_EDGE",EDGE,{"disambiguationData":[OSD([sQuery(id+"F2.wireOp",EDGE,"E13.19.2")])],"isStart":false});
            var Q50;
            Q50=makeQuery(id+"F3.opExtrude","CAP_EDGE",EDGE,{"disambiguationData":[OSD([sQuery(id+"F2.wireOp",EDGE,"E10.trimOffspring")])],"isStart":false});
            var Q51;
            Q51=makeQuery(id+"F3.opExtrude","CAP_EDGE",EDGE,{"disambiguationData":[OSD([sQuery(id+"F2.wireOp",EDGE,"E11.MirrorCS")])],"isStart":false});
            var Q52;
            {var subQ0=sQuery(id+"F2.wireOp",EDGE,"E0");Q52=makeQuery(id+"F3.opExtrude","CAP_EDGE",EDGE,{"disambiguationData":[OSD([subQ0]),TDD([makeQuery(id+"F2.imprint","IMPRINT",EDGE,{"disambiguationData":[TD([[makeQuery(id+"F2.imprint","INTERSECT",VERTEX,{"derivedFrom":[subQ0,sQuery(id+"F2.wireOp",EDGE,"E11.MirrorCS")]}),-1.0]])],"derivedFrom":subQ0})])],"isStart":false});}
            var Q53;
            Q53=makeQuery(id+"F3.opExtrude","CAP_EDGE",EDGE,{"disambiguationData":[OSD([sQuery(id+"F2.wireOp",EDGE,"E13.1.0")])],"isStart":false});
            var Q54;
            Q54=makeQuery(id+"F3.opExtrude","CAP_EDGE",EDGE,{"disambiguationData":[OSD([sQuery(id+"F2.wireOp",EDGE,"E13.1.2")])],"isStart":false});
            var Q55;
            {var subQ0=sQuery(id+"F2.wireOp",EDGE,"E0");Q55=makeQuery(id+"F3.opExtrude","CAP_EDGE",EDGE,{"disambiguationData":[OSD([subQ0]),TDD([makeQuery(id+"F2.imprint","IMPRINT",EDGE,{"disambiguationData":[TD([[makeQuery(id+"F2.imprint","INTERSECT",VERTEX,{"derivedFrom":[subQ0,sQuery(id+"F2.wireOp",EDGE,"E13.1.2")]}),-1.0]])],"derivedFrom":subQ0})])],"isStart":false});}
            var Q56;
            Q56=makeQuery(id+"F3.opExtrude","CAP_EDGE",EDGE,{"disambiguationData":[OSD([sQuery(id+"F2.wireOp",EDGE,"E13.2.0")])],"isStart":false});
            var Q57;
            Q57=makeQuery(id+"F3.opExtrude","CAP_EDGE",EDGE,{"disambiguationData":[OSD([sQuery(id+"F2.wireOp",EDGE,"E13.2.2")])],"isStart":false});
            var Q58;
            {var subQ0=sQuery(id+"F2.wireOp",EDGE,"E0");Q58=makeQuery(id+"F3.opExtrude","CAP_EDGE",EDGE,{"disambiguationData":[OSD([subQ0]),TDD([makeQuery(id+"F2.imprint","IMPRINT",EDGE,{"disambiguationData":[TD([[makeQuery(id+"F2.imprint","INTERSECT",VERTEX,{"derivedFrom":[subQ0,sQuery(id+"F2.wireOp",EDGE,"E13.2.2")]}),-1.0]])],"derivedFrom":subQ0})])],"isStart":false});}
            var Q59;
            Q59=makeQuery(id+"F3.opExtrude","CAP_EDGE",EDGE,{"disambiguationData":[OSD([sQuery(id+"F2.wireOp",EDGE,"E13.3.0")])],"isStart":false});
            var Q60;
            Q60=makeQuery(id+"F3.opExtrude","CAP_EDGE",EDGE,{"disambiguationData":[OSD([sQuery(id+"F2.wireOp",EDGE,"E13.3.2")])],"isStart":false});
            var Q61;
            {var subQ0=sQuery(id+"F2.wireOp",EDGE,"E0");Q61=makeQuery(id+"F3.opExtrude","CAP_EDGE",EDGE,{"disambiguationData":[OSD([subQ0]),TDD([makeQuery(id+"F2.imprint","IMPRINT",EDGE,{"disambiguationData":[TD([[makeQuery(id+"F2.imprint","INTERSECT",VERTEX,{"derivedFrom":[subQ0,sQuery(id+"F2.wireOp",EDGE,"E13.3.2")]}),-1.0]])],"derivedFrom":subQ0})])],"isStart":false});}
            var Q62;
            Q62=makeQuery(id+"F3.opExtrude","CAP_EDGE",EDGE,{"disambiguationData":[OSD([sQuery(id+"F2.wireOp",EDGE,"E13.4.0")])],"isStart":false});
            var Q63;
            Q63=makeQuery(id+"F3.opExtrude","CAP_EDGE",EDGE,{"disambiguationData":[OSD([sQuery(id+"F2.wireOp",EDGE,"E13.4.2")])],"isStart":false});
            var Q64;
            {var subQ0=sQuery(id+"F2.wireOp",EDGE,"E0");Q64=makeQuery(id+"F3.opExtrude","CAP_EDGE",EDGE,{"disambiguationData":[OSD([subQ0]),TDD([makeQuery(id+"F2.imprint","IMPRINT",EDGE,{"disambiguationData":[TD([[makeQuery(id+"F2.imprint","INTERSECT",VERTEX,{"derivedFrom":[subQ0,sQuery(id+"F2.wireOp",EDGE,"E13.4.2")]}),-1.0]])],"derivedFrom":subQ0})])],"isStart":false});}
            var Q65;
            {var subQ0=sQuery(id+"F2.wireOp",EDGE,"E0");Q65=makeQuery(id+"F3.opExtrude","CAP_EDGE",EDGE,{"disambiguationData":[OSD([subQ0]),TDD([makeQuery(id+"F2.imprint","IMPRINT",EDGE,{"disambiguationData":[TD([[makeQuery(id+"F2.imprint","INTERSECT",VERTEX,{"derivedFrom":[subQ0,sQuery(id+"F2.wireOp",EDGE,"E13.5.2")]}),-1.0]])],"derivedFrom":subQ0})])],"isStart":true});}
            var Q66;
            Q66=makeQuery(id+"F3.opExtrude","CAP_EDGE",EDGE,{"disambiguationData":[OSD([sQuery(id+"F2.wireOp",EDGE,"E13.5.2")])],"isStart":true});
            var Q67;
            {var subQ0=sQuery(id+"F2.wireOp",EDGE,"E0");Q67=makeQuery(id+"F3.opExtrude","CAP_EDGE",EDGE,{"disambiguationData":[OSD([subQ0]),TDD([makeQuery(id+"F2.imprint","IMPRINT",EDGE,{"disambiguationData":[TD([[makeQuery(id+"F2.imprint","INTERSECT",VERTEX,{"derivedFrom":[subQ0,sQuery(id+"F2.wireOp",EDGE,"E13.4.2")]}),-1.0]])],"derivedFrom":subQ0})])],"isStart":true});}
            var Q68;
            Q68=makeQuery(id+"F3.opExtrude","CAP_EDGE",EDGE,{"disambiguationData":[OSD([sQuery(id+"F2.wireOp",EDGE,"E13.4.2")])],"isStart":true});
            var Q69;
            Q69=makeQuery(id+"F3.opExtrude","CAP_EDGE",EDGE,{"disambiguationData":[OSD([sQuery(id+"F2.wireOp",EDGE,"E13.4.0")])],"isStart":true});
            var Q70;
            {var subQ0=sQuery(id+"F2.wireOp",EDGE,"E0");Q70=makeQuery(id+"F3.opExtrude","CAP_EDGE",EDGE,{"disambiguationData":[OSD([subQ0]),TDD([makeQuery(id+"F2.imprint","IMPRINT",EDGE,{"disambiguationData":[TD([[makeQuery(id+"F2.imprint","INTERSECT",VERTEX,{"derivedFrom":[subQ0,sQuery(id+"F2.wireOp",EDGE,"E13.3.2")]}),-1.0]])],"derivedFrom":subQ0})])],"isStart":true});}
            var Q71;
            Q71=makeQuery(id+"F3.opExtrude","CAP_EDGE",EDGE,{"disambiguationData":[OSD([sQuery(id+"F2.wireOp",EDGE,"E13.3.2")])],"isStart":true});
            var Q72;
            Q72=makeQuery(id+"F3.opExtrude","CAP_EDGE",EDGE,{"disambiguationData":[OSD([sQuery(id+"F2.wireOp",EDGE,"E13.3.0")])],"isStart":true});
            var Q73;
            {var subQ0=sQuery(id+"F2.wireOp",EDGE,"E0");Q73=makeQuery(id+"F3.opExtrude","CAP_EDGE",EDGE,{"disambiguationData":[OSD([subQ0]),TDD([makeQuery(id+"F2.imprint","IMPRINT",EDGE,{"disambiguationData":[TD([[makeQuery(id+"F2.imprint","INTERSECT",VERTEX,{"derivedFrom":[subQ0,sQuery(id+"F2.wireOp",EDGE,"E13.2.2")]}),-1.0]])],"derivedFrom":subQ0})])],"isStart":true});}
            var Q74;
            Q74=makeQuery(id+"F3.opExtrude","CAP_EDGE",EDGE,{"disambiguationData":[OSD([sQuery(id+"F2.wireOp",EDGE,"E13.2.2")])],"isStart":true});
            var Q75;
            Q75=makeQuery(id+"F3.opExtrude","CAP_EDGE",EDGE,{"disambiguationData":[OSD([sQuery(id+"F2.wireOp",EDGE,"E13.2.0")])],"isStart":true});
            var Q76;
            Q76=makeQuery(id+"F3.opExtrude","CAP_EDGE",EDGE,{"disambiguationData":[OSD([sQuery(id+"F2.wireOp",EDGE,"E13.1.2")])],"isStart":true});
            var Q77;
            {var subQ0=sQuery(id+"F2.wireOp",EDGE,"E0");Q77=makeQuery(id+"F3.opExtrude","CAP_EDGE",EDGE,{"disambiguationData":[OSD([subQ0]),TDD([makeQuery(id+"F2.imprint","IMPRINT",EDGE,{"disambiguationData":[TD([[makeQuery(id+"F2.imprint","INTERSECT",VERTEX,{"derivedFrom":[subQ0,sQuery(id+"F2.wireOp",EDGE,"E13.1.2")]}),-1.0]])],"derivedFrom":subQ0})])],"isStart":true});}
            var Q78;
            Q78=makeQuery(id+"F3.opExtrude","CAP_EDGE",EDGE,{"disambiguationData":[OSD([sQuery(id+"F2.wireOp",EDGE,"E13.1.0")])],"isStart":true});
            var Q79;
            {var subQ0=sQuery(id+"F2.wireOp",EDGE,"E0");Q79=makeQuery(id+"F3.opExtrude","CAP_EDGE",EDGE,{"disambiguationData":[OSD([subQ0]),TDD([makeQuery(id+"F2.imprint","IMPRINT",EDGE,{"disambiguationData":[TD([[makeQuery(id+"F2.imprint","INTERSECT",VERTEX,{"derivedFrom":[subQ0,sQuery(id+"F2.wireOp",EDGE,"E11.MirrorCS")]}),-1.0]])],"derivedFrom":subQ0})])],"isStart":true});}
            var Q80;
            Q80=makeQuery(id+"F3.opExtrude","CAP_EDGE",EDGE,{"disambiguationData":[OSD([sQuery(id+"F2.wireOp",EDGE,"E11.MirrorCS")])],"isStart":true});
            var Q81;
            Q81=makeQuery(id+"F3.opExtrude","CAP_EDGE",EDGE,{"disambiguationData":[OSD([sQuery(id+"F2.wireOp",EDGE,"E10.trimOffspring")])],"isStart":true});
            var Q82;
            {var subQ0=sQuery(id+"F2.wireOp",EDGE,"E0");Q82=makeQuery(id+"F3.opExtrude","CAP_EDGE",EDGE,{"disambiguationData":[OSD([subQ0]),TDD([makeQuery(id+"F2.imprint","IMPRINT",EDGE,{"disambiguationData":[TD([[makeQuery(id+"F2.imprint","INTERSECT",VERTEX,{"derivedFrom":[subQ0,sQuery(id+"F2.wireOp",EDGE,"E10.trimOffspring")]}),1.0]])],"derivedFrom":subQ0})])],"isStart":true});}
            var Q83;
            Q83=makeQuery(id+"F3.opExtrude","CAP_EDGE",EDGE,{"disambiguationData":[OSD([sQuery(id+"F2.wireOp",EDGE,"E13.19.2")])],"isStart":true});
            var Q84;
            Q84=makeQuery(id+"F3.opExtrude","CAP_EDGE",EDGE,{"disambiguationData":[OSD([sQuery(id+"F2.wireOp",EDGE,"E13.19.0")])],"isStart":true});
            var Q85;
            {var subQ0=sQuery(id+"F2.wireOp",EDGE,"E0");Q85=makeQuery(id+"F3.opExtrude","CAP_EDGE",EDGE,{"disambiguationData":[OSD([subQ0]),TDD([makeQuery(id+"F2.imprint","IMPRINT",EDGE,{"disambiguationData":[TD([[makeQuery(id+"F2.imprint","INTERSECT",VERTEX,{"derivedFrom":[subQ0,sQuery(id+"F2.wireOp",EDGE,"E13.18.2")]}),-1.0]])],"derivedFrom":subQ0})])],"isStart":true});}
            var Q86;
            Q86=makeQuery(id+"F3.opExtrude","CAP_EDGE",EDGE,{"disambiguationData":[OSD([sQuery(id+"F2.wireOp",EDGE,"E13.18.2")])],"isStart":true});
            var Q87;
            Q87=makeQuery(id+"F3.opExtrude","CAP_EDGE",EDGE,{"disambiguationData":[OSD([sQuery(id+"F2.wireOp",EDGE,"E13.18.0")])],"isStart":true});
            var Q88;
            {var subQ0=sQuery(id+"F2.wireOp",EDGE,"E0");Q88=makeQuery(id+"F3.opExtrude","CAP_EDGE",EDGE,{"disambiguationData":[OSD([subQ0]),TDD([makeQuery(id+"F2.imprint","IMPRINT",EDGE,{"disambiguationData":[TD([[makeQuery(id+"F2.imprint","INTERSECT",VERTEX,{"derivedFrom":[subQ0,sQuery(id+"F2.wireOp",EDGE,"E13.17.2")]}),-1.0]])],"derivedFrom":subQ0})])],"isStart":true});}
            var Q89;
            Q89=makeQuery(id+"F3.opExtrude","CAP_EDGE",EDGE,{"disambiguationData":[OSD([sQuery(id+"F2.wireOp",EDGE,"E13.17.2")])],"isStart":true});
            var Q90;
            Q90=makeQuery(id+"F3.opExtrude","CAP_EDGE",EDGE,{"disambiguationData":[OSD([sQuery(id+"F2.wireOp",EDGE,"E13.17.0")])],"isStart":true});
            var Q91;
            {var subQ0=sQuery(id+"F2.wireOp",EDGE,"E0");Q91=makeQuery(id+"F3.opExtrude","CAP_EDGE",EDGE,{"disambiguationData":[OSD([subQ0]),TDD([makeQuery(id+"F2.imprint","IMPRINT",EDGE,{"disambiguationData":[TD([[makeQuery(id+"F2.imprint","INTERSECT",VERTEX,{"derivedFrom":[subQ0,sQuery(id+"F2.wireOp",EDGE,"E13.16.2")]}),-1.0]])],"derivedFrom":subQ0})])],"isStart":true});}
            var Q92;
            Q92=makeQuery(id+"F3.opExtrude","CAP_EDGE",EDGE,{"disambiguationData":[OSD([sQuery(id+"F2.wireOp",EDGE,"E13.16.2")])],"isStart":true});
            var Q93;
            Q93=makeQuery(id+"F3.opExtrude","CAP_EDGE",EDGE,{"disambiguationData":[OSD([sQuery(id+"F2.wireOp",EDGE,"E13.16.0")])],"isStart":true});
            var Q94;
            {var subQ0=sQuery(id+"F2.wireOp",EDGE,"E0");Q94=makeQuery(id+"F3.opExtrude","CAP_EDGE",EDGE,{"disambiguationData":[OSD([subQ0]),TDD([makeQuery(id+"F2.imprint","IMPRINT",EDGE,{"disambiguationData":[TD([[makeQuery(id+"F2.imprint","INTERSECT",VERTEX,{"derivedFrom":[subQ0,sQuery(id+"F2.wireOp",EDGE,"E13.15.2")]}),-1.0]])],"derivedFrom":subQ0})])],"isStart":true});}
            var Q95;
            Q95=makeQuery(id+"F3.opExtrude","CAP_EDGE",EDGE,{"disambiguationData":[OSD([sQuery(id+"F2.wireOp",EDGE,"E13.15.2")])],"isStart":true});
            var Q96;
            Q96=makeQuery(id+"F3.opExtrude","CAP_EDGE",EDGE,{"disambiguationData":[OSD([sQuery(id+"F2.wireOp",EDGE,"E13.15.0")])],"isStart":true});
            var Q97;
            {var subQ0=sQuery(id+"F2.wireOp",EDGE,"E0");Q97=makeQuery(id+"F3.opExtrude","CAP_EDGE",EDGE,{"disambiguationData":[OSD([subQ0]),TDD([makeQuery(id+"F2.imprint","IMPRINT",EDGE,{"disambiguationData":[TD([[makeQuery(id+"F2.imprint","INTERSECT",VERTEX,{"derivedFrom":[subQ0,sQuery(id+"F2.wireOp",EDGE,"E13.14.2")]}),-1.0]])],"derivedFrom":subQ0})])],"isStart":true});}
            var Q98;
            Q98=makeQuery(id+"F3.opExtrude","CAP_EDGE",EDGE,{"disambiguationData":[OSD([sQuery(id+"F2.wireOp",EDGE,"E13.14.2")])],"isStart":true});
            var Q99;
            Q99=makeQuery(id+"F3.opExtrude","CAP_EDGE",EDGE,{"disambiguationData":[OSD([sQuery(id+"F2.wireOp",EDGE,"E13.14.0")])],"isStart":true});
            var Q100;
            {var subQ0=sQuery(id+"F2.wireOp",EDGE,"E0");Q100=makeQuery(id+"F3.opExtrude","CAP_EDGE",EDGE,{"disambiguationData":[OSD([subQ0]),TDD([makeQuery(id+"F2.imprint","IMPRINT",EDGE,{"disambiguationData":[TD([[makeQuery(id+"F2.imprint","INTERSECT",VERTEX,{"derivedFrom":[subQ0,sQuery(id+"F2.wireOp",EDGE,"E13.13.2")]}),-1.0]])],"derivedFrom":subQ0})])],"isStart":true});}
            var Q101;
            Q101=makeQuery(id+"F3.opExtrude","CAP_EDGE",EDGE,{"disambiguationData":[OSD([sQuery(id+"F2.wireOp",EDGE,"E13.13.2")])],"isStart":true});
            var Q102;
            Q102=makeQuery(id+"F3.opExtrude","CAP_EDGE",EDGE,{"disambiguationData":[OSD([sQuery(id+"F2.wireOp",EDGE,"E13.13.0")])],"isStart":true});
            var Q103;
            {var subQ0=sQuery(id+"F2.wireOp",EDGE,"E0");Q103=makeQuery(id+"F3.opExtrude","CAP_EDGE",EDGE,{"disambiguationData":[OSD([subQ0]),TDD([makeQuery(id+"F2.imprint","IMPRINT",EDGE,{"disambiguationData":[TD([[makeQuery(id+"F2.imprint","INTERSECT",VERTEX,{"derivedFrom":[subQ0,sQuery(id+"F2.wireOp",EDGE,"E13.12.2")]}),-1.0]])],"derivedFrom":subQ0})])],"isStart":true});}
            var Q104;
            Q104=makeQuery(id+"F3.opExtrude","CAP_EDGE",EDGE,{"disambiguationData":[OSD([sQuery(id+"F2.wireOp",EDGE,"E13.12.2")])],"isStart":true});
            var Q105;
            Q105=makeQuery(id+"F3.opExtrude","CAP_EDGE",EDGE,{"disambiguationData":[OSD([sQuery(id+"F2.wireOp",EDGE,"E13.12.0")])],"isStart":true});
            var Q106;
            {var subQ0=sQuery(id+"F2.wireOp",EDGE,"E0");Q106=makeQuery(id+"F3.opExtrude","CAP_EDGE",EDGE,{"disambiguationData":[OSD([subQ0]),TDD([makeQuery(id+"F2.imprint","IMPRINT",EDGE,{"disambiguationData":[TD([[makeQuery(id+"F2.imprint","INTERSECT",VERTEX,{"derivedFrom":[subQ0,sQuery(id+"F2.wireOp",EDGE,"E13.11.2")]}),-1.0]])],"derivedFrom":subQ0})])],"isStart":true});}
            var Q107;
            Q107=makeQuery(id+"F3.opExtrude","CAP_EDGE",EDGE,{"disambiguationData":[OSD([sQuery(id+"F2.wireOp",EDGE,"E13.11.2")])],"isStart":true});
            var Q108;
            Q108=makeQuery(id+"F3.opExtrude","CAP_EDGE",EDGE,{"disambiguationData":[OSD([sQuery(id+"F2.wireOp",EDGE,"E13.11.0")])],"isStart":true});
            var Q109;
            {var subQ0=sQuery(id+"F2.wireOp",EDGE,"E0");Q109=makeQuery(id+"F3.opExtrude","CAP_EDGE",EDGE,{"disambiguationData":[OSD([subQ0]),TDD([makeQuery(id+"F2.imprint","IMPRINT",EDGE,{"disambiguationData":[TD([[makeQuery(id+"F2.imprint","INTERSECT",VERTEX,{"derivedFrom":[subQ0,sQuery(id+"F2.wireOp",EDGE,"E13.10.2")]}),-1.0]])],"derivedFrom":subQ0})])],"isStart":true});}
            var Q110;
            Q110=makeQuery(id+"F3.opExtrude","CAP_EDGE",EDGE,{"disambiguationData":[OSD([sQuery(id+"F2.wireOp",EDGE,"E13.10.2")])],"isStart":true});
            var Q111;
            Q111=makeQuery(id+"F3.opExtrude","CAP_EDGE",EDGE,{"disambiguationData":[OSD([sQuery(id+"F2.wireOp",EDGE,"E13.10.0")])],"isStart":true});
            var Q112;
            {var subQ0=sQuery(id+"F2.wireOp",EDGE,"E0");Q112=makeQuery(id+"F3.opExtrude","CAP_EDGE",EDGE,{"disambiguationData":[OSD([subQ0]),TDD([makeQuery(id+"F2.imprint","IMPRINT",EDGE,{"disambiguationData":[TD([[makeQuery(id+"F2.imprint","INTERSECT",VERTEX,{"derivedFrom":[subQ0,sQuery(id+"F2.wireOp",EDGE,"E13.9.2")]}),-1.0]])],"derivedFrom":subQ0})])],"isStart":true});}
            var Q113;
            Q113=makeQuery(id+"F3.opExtrude","CAP_EDGE",EDGE,{"disambiguationData":[OSD([sQuery(id+"F2.wireOp",EDGE,"E13.9.2")])],"isStart":true});
            var Q114;
            Q114=makeQuery(id+"F3.opExtrude","CAP_EDGE",EDGE,{"disambiguationData":[OSD([sQuery(id+"F2.wireOp",EDGE,"E13.9.0")])],"isStart":true});
            var Q115;
            {var subQ0=sQuery(id+"F2.wireOp",EDGE,"E0");Q115=makeQuery(id+"F3.opExtrude","CAP_EDGE",EDGE,{"disambiguationData":[OSD([subQ0]),TDD([makeQuery(id+"F2.imprint","IMPRINT",EDGE,{"disambiguationData":[TD([[makeQuery(id+"F2.imprint","INTERSECT",VERTEX,{"derivedFrom":[subQ0,sQuery(id+"F2.wireOp",EDGE,"E13.8.2")]}),-1.0]])],"derivedFrom":subQ0})])],"isStart":true});}
            var Q116;
            Q116=makeQuery(id+"F3.opExtrude","CAP_EDGE",EDGE,{"disambiguationData":[OSD([sQuery(id+"F2.wireOp",EDGE,"E13.8.2")])],"isStart":true});
            fillet(context, id + "F4", {"entities" : qUnion([Q0, Q1, Q2, Q3, Q4, Q5, Q6, Q7, Q8, Q9, Q10, Q11, Q12, Q13, Q14, Q15, Q16, Q17, Q18, Q19, Q20, Q21, Q22, Q23, Q24, Q25, Q26, Q27, Q28, Q29, Q30, Q31, Q32, Q33, Q34, Q35, Q36, Q37, Q38, Q39, Q40, Q41, Q42, Q43, Q44, Q45, Q46, Q47, Q48, Q49, Q50, Q51, Q52, Q53, Q54, Q55, Q56, Q57, Q58, Q59, Q60, Q61, Q62, Q63, Q64, Q65, Q66, Q67, Q68, Q69, Q70, Q71, Q72, Q73, Q74, Q75, Q76, Q77, Q78, Q79, Q80, Q81, Q82, Q83, Q84, Q85, Q86, Q87, Q88, Q89, Q90, Q91, Q92, Q93, Q94, Q95, Q96, Q97, Q98, Q99, Q100, Q101, Q102, Q103, Q104, Q105, Q106, Q107, Q108, Q109, Q110, Q111, Q112, Q113, Q114, Q115, Q116]), "radius" : (getVariable(context, 'TeethFillet')) * mm, "tangentPropagation" : true, "allowEdgeOverflow" : false});
        }
    });
